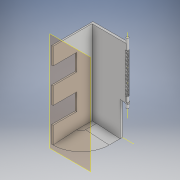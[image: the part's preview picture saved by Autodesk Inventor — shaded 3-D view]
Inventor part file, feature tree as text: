
AUTODESK INVENTOR PART (.ipt)
format: ipt  version: 2018 (Build 220112000, 112)  size: 846,848 bytes
history: native  units: mm
features: sketch x11, extrude x11, plane x6, other x4, pattern_circular x1, fillet x1, chamfer x1, mirror x1, projected_geometry x1
ambient origin geometry x8: Origin, YZ Plane, XZ Plane, XY Plane, X Axis, Y Axis, Z Axis, Center Point
bodies: Body1 (feature_tree)
feature tree (37):
  other  "Sólido1"
  sketch  "Boceto1"  dims[d0=100.0mm d1=145.0mm]
  extrude  "Extrusión2"  Depth=145.0mm
  extrude  "Extrusión3"  Depth=20.0mm
  plane  "Plano de trabajo1"
  extrude  "Extrusión4"  Depth=2.5mm TaperAngle=0.0deg
  extrude  "Extrusión5"  Depth=50.0mm TaperAngle=0.0deg
  extrude  "Extrusión6"  Depth=3.0mm
  sketch  "Boceto5"  dims[d29=0.0mm d31=50.0mm d32=0.0mm]
  extrude  "Extrusión8"  Depth=3.0mm
  extrude  "Extrusión9"  Depth=3.0mm
  plane  "Plano de trabajo2"
  other  "Bobina1"
  other  "Eje de trabajo1"
  pattern_circular  "Patrón circular1"  [2 undecoded]
  fillet  "Empalme1"  Radius=0.5mm
  chamfer  "Chaflán4"  Distance=2.0mm
  extrude  "Extrusión10"  Depth=2.0mm
  extrude  "Extrusión11"  Depth=2.0mm TaperAngle=360.0deg
  sketch  "Boceto10"  dims[d50=0.0mm d51=0.0mm]
  plane  "Plano de trabajo4"
  extrude  "Extrusión12"  Depth=2.0mm
  mirror  "Simetría1"
  plane  "Plano de trabajo5"
  plane  "Plano de trabajo6"
  extrude  "Extrusión13"  Depth=2.5mm TaperAngle=45.0deg
  plane  "Plano de trabajo7"
  sketch  "Boceto2"  dims[d2=4.0mm d12=20.0mm]
  sketch  "Boceto3"  dims[d25=2.5mm d26=0.0mm d27=50.0mm d28=0.0mm]
  projected_geometry  "Contorno proyectado1"
  sketch  "Boceto6"  dims[d33=2.5mm d34=0.0mm d38=3.0mm]
  sketch  "Boceto7"  dims[d42=12.5mm d43=0.0mm d44=3.0mm]
  sketch  "Boceto8"  dims[d45=3.0mm d48=12.5mm]
  sketch  "Boceto9"  dims[d49=12.5mm]
  sketch  "Boceto11"  dims[d52=4.0mm]
  other  "Eje de trabajo3"
  sketch  "Boceto12"  dims[d53=15.0mm d54=0.0mm d56=2.0mm d57=0.5mm d58=2.0mm d59=0.5mm d60=10.0mm d61=100.0mm d62=200.0mm d63=0.0mm d64=90.0deg d65=90.0deg d66=0.0mm d67=0.0mm d68=50.0mm d69=360.0deg d71=47.5mm d75=2.5mm d76=40.0mm d77=45.0deg d78=4.0mm d79=10.0mm d80=0.0mm d81=4.0mm d82=8.0mm d83=0.0mm d85=50.0mm d86=90.0deg d88=1.5mm d89=1.5mm d90=2.499964mm d91=10.0mm d92=0.0mm d93=29.0mm d94=29.0mm d95=29.0mm d97=29.0mm d98=100.0mm d99=100.0mm d100=4.0mm d101=4.0mm d102=6.0mm d103=2.0mm d104=0.0mm]
note: 2 required parameter values undecoded (feature->parameter linkage not recoverable at this tier; creation-order binding heuristic only, values carry confidence <= 0.55)
